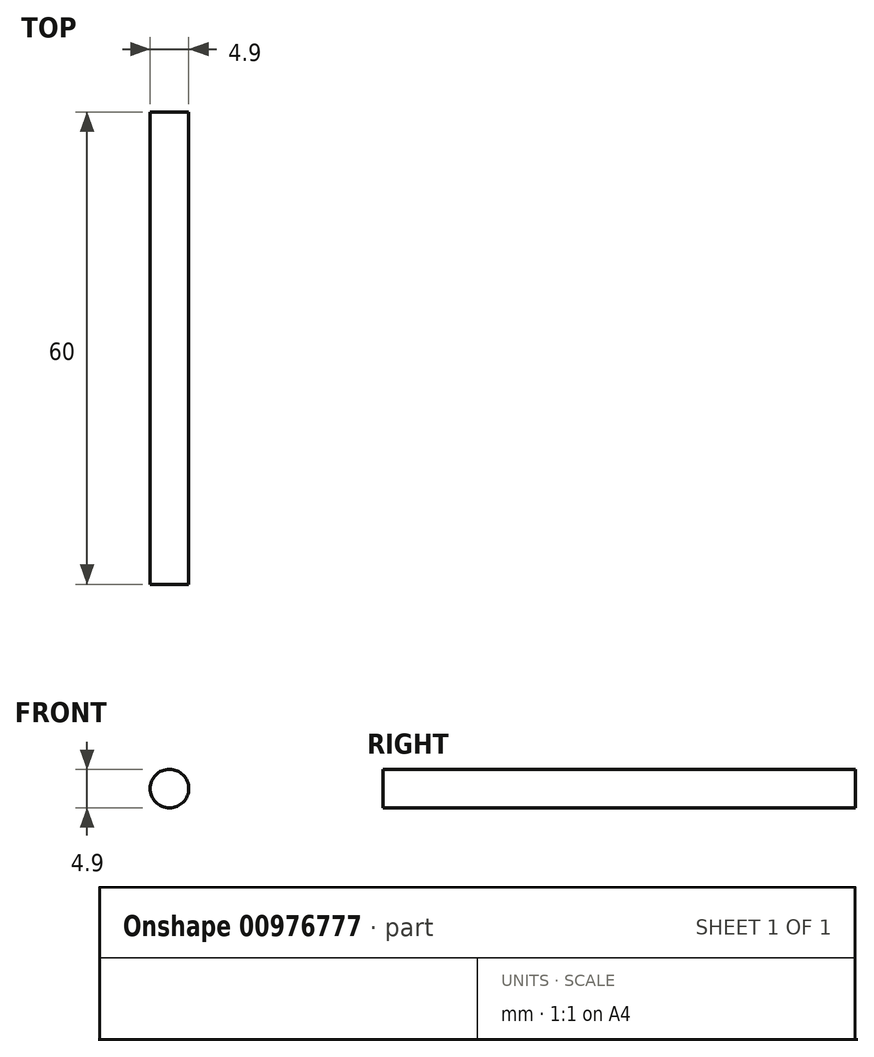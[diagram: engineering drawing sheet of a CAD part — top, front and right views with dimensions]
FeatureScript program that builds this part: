
annotation { "Feature Type Name" : "Feature", "Feature Type Description" : "" }
export const myFeature = defineFeature(function(context is Context, id is Id, definition is map)
    precondition{}
    {
        {
            var Q0;
            Q0=qCreatedBy(makeId("Front.planeOp"),FACE);
            var sketch = newSketch(context, id + "F0", { "sketchPlane" : qUnion([Q0])});
            skCircle(sketch, "E0", {"center": v(0, 0) * mm, "radius": 2.45 * mm});
            skSolve(sketch);
        }
        {
            var Q0;
            Q0=makeQuery(id+"F0.imprint","IMPRINT",FACE,{"disambiguationData":[TD([[makeQuery(id+"F0.imprint","IMPRINT",EDGE,{"derivedFrom":sQuery(id+"F0.wireOp",EDGE,"E0")}),1.0]])]});
            extrude(context, id + "F1", {"entities" : qUnion([Q0]), "depth" : 60 * mm, "offsetDistance" : 25 * mm});
        }
    });
